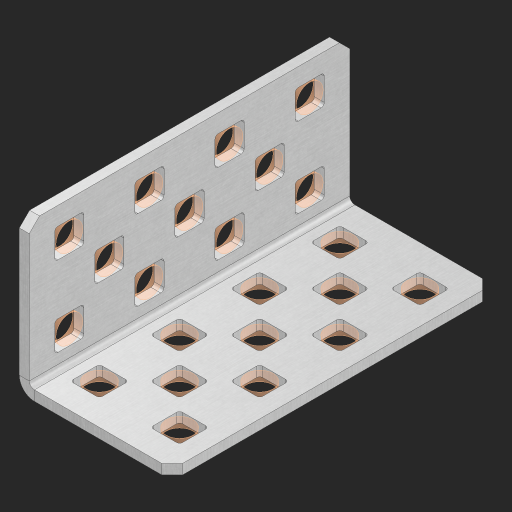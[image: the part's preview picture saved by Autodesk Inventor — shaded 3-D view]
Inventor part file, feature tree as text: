
AUTODESK INVENTOR PART (.ipt)
format: ipt  version: 2023 (Build 270158000, 158)  size: 559,104 bytes
history: native  units: in
note: dims shown in document units (in); Inventor stores cm internally (conversion verified against a paired STEP export)
features: other x23, extrude x22, pattern_linear x4, sketch x4, chamfer x1, imported_body x1
ambient origin geometry x8: Origin, YZ Plane, XZ Plane, XY Plane, X Axis, Y Axis, Z Axis, Center Point
bodies: Body1 (feature_tree), Body2 (feature_tree), Body3 (feature_tree), Body4 (feature_tree), Body5 (feature_tree), Body6 (feature_tree), Body7 (feature_tree), Body8 (feature_tree), Body9 (feature_tree), Body10 (feature_tree), Body11 (feature_tree), Body12 (feature_tree), Body13 (feature_tree), Body14 (feature_tree), Body15 (feature_tree), Body16 (feature_tree), Body17 (feature_tree), Body18 (feature_tree), Body19 (feature_tree), Body20 (feature_tree), Body21 (feature_tree), Body22 (feature_tree), Body23 (feature_tree)
feature tree (55):
  other  "Angle Coupler Gusset"
  chamfer  "Chamfer2"  Distance=0.062in
  pattern_linear  "Rectangular Pattern1"  Count1=4 Spacing1=0.5in
  pattern_linear  "Rectangular Pattern2"  Count1=2 Spacing1=0.5in
  pattern_linear  "Rectangular Pattern3"  Count1=3 Spacing1=0.5in
  pattern_linear  "Rectangular Pattern4"  Count1=2 Spacing1=0.5in
  imported_body  "Base1"
  sketch  "Sketch1"  dims[d10=0.062in d11=0.0in d12=1.1811in d14=0.5in]
  other  "Srf1"
  other  "Srf2"
  other  "Srf3"
  other  "Srf4"
  other  "Srf5"
  other  "Srf6"
  other  "Srf7"
  other  "Srf8"
  sketch  "Sketch2"  dims[d16=0.062in d17=0.0in d18=0.7874in d20=0.5in]
  other  "Srf9"
  other  "Srf10"
  other  "Srf11"
  sketch  "Sketch3"  dims[d21=1.5748in d23=0.5in d25=0.062in d26=0.0in]
  other  "Srf12"
  other  "Srf13"
  other  "Srf14"
  other  "Srf15"
  other  "Srf16"
  other  "Srf17"
  other  "Srf18"
  other  "Srf19"
  sketch  "Sketch4"  dims[d27=1.1811in d29=0.5in]
  other  "Srf20"
  other  "Srf21"
  other  "Srf22"
  extrude  "ExtrusionSrf1"  Depth=0.062in TaperAngle=0.0deg
  extrude  "ExtrusionSrf9"  [1 undecoded]
  extrude  "ExtrusionSrf12"  [1 undecoded]
  extrude  "ExtrusionSrf20"  [1 undecoded]
  extrude  "ExtrusionSrf2"  [1 undecoded]
  extrude  "ExtrusionSrf3"  [1 undecoded]
  extrude  "ExtrusionSrf4"  [1 undecoded]
  extrude  "ExtrusionSrf5"  [1 undecoded]
  extrude  "ExtrusionSrf6"  [1 undecoded]
  extrude  "ExtrusionSrf7"  [1 undecoded]
  extrude  "ExtrusionSrf8"  [1 undecoded]
  extrude  "ExtrusionSrf10"  [1 undecoded]
  extrude  "ExtrusionSrf11"  [1 undecoded]
  extrude  "ExtrusionSrf13"  [1 undecoded]
  extrude  "ExtrusionSrf14"  [1 undecoded]
  extrude  "ExtrusionSrf15"  [1 undecoded]
  extrude  "ExtrusionSrf16"  [1 undecoded]
  extrude  "ExtrusionSrf17"  [1 undecoded]
  extrude  "ExtrusionSrf18"  [1 undecoded]
  extrude  "ExtrusionSrf19"  [1 undecoded]
  extrude  "ExtrusionSrf21"  [1 undecoded]
  extrude  "ExtrusionSrf22"  [1 undecoded]
note: 21 required parameter values undecoded (feature->parameter linkage not recoverable at this tier; creation-order binding heuristic only, values carry confidence <= 0.55)
